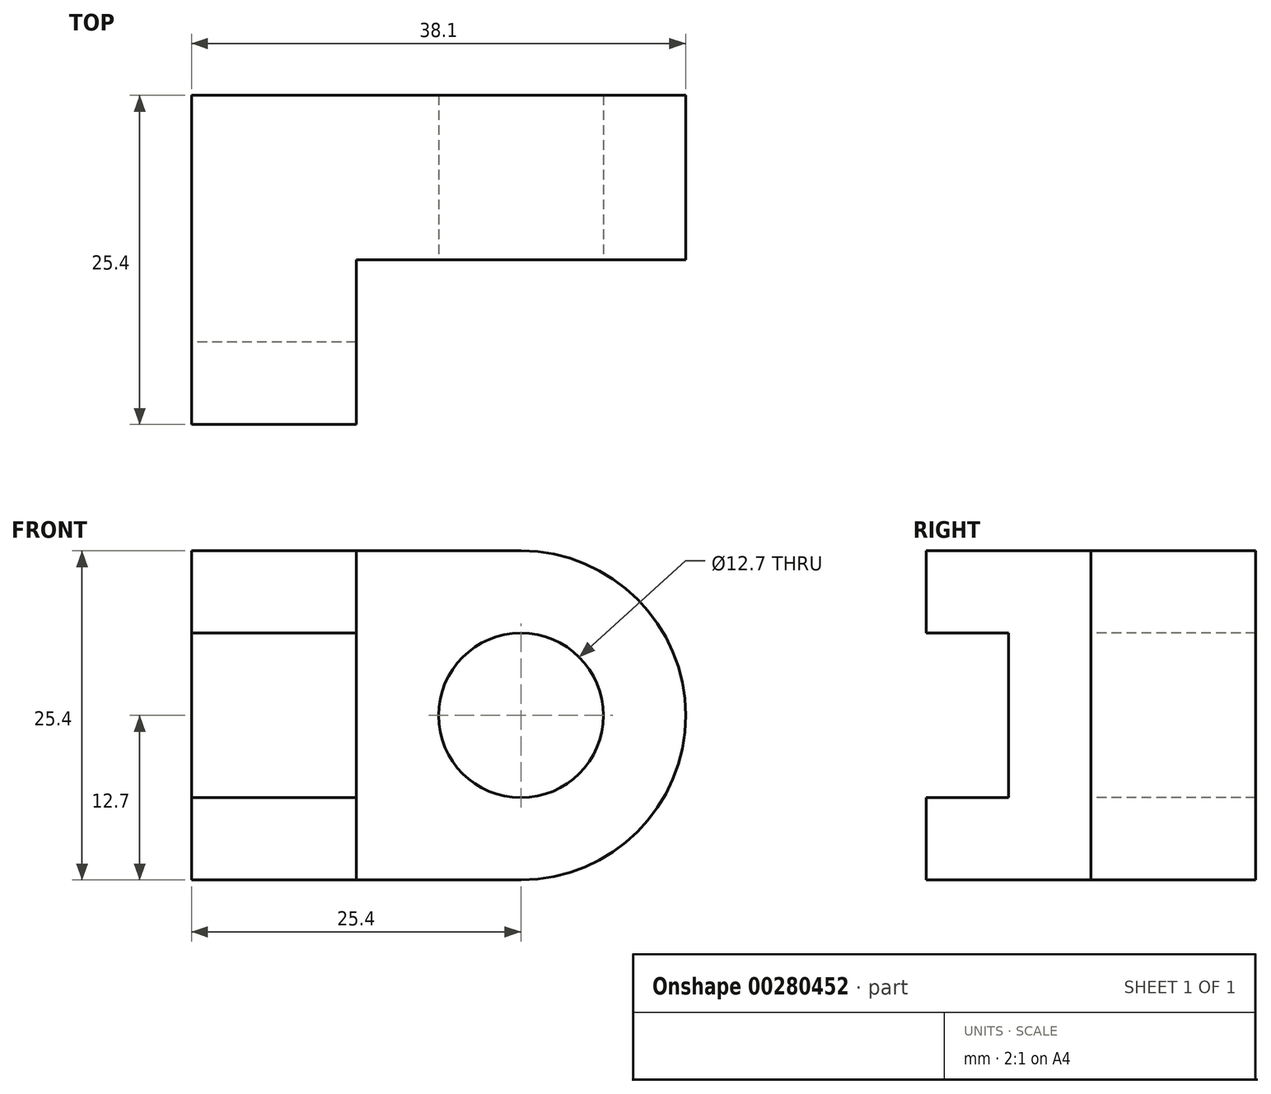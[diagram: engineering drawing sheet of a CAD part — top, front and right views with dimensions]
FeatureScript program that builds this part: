
annotation { "Feature Type Name" : "Feature", "Feature Type Description" : "" }
export const myFeature = defineFeature(function(context is Context, id is Id, definition is map)
    precondition{}
    {
        {
            var Q0;
            Q0=qCreatedBy(makeId("Top.planeOp"),FACE);
            var sketch = newSketch(context, id + "F0", { "sketchPlane" : qUnion([Q0])});
            skLineSegment(sketch, "E0", {"start": v(0, 0) * mm, "end": v(12.7, 0) * mm});
            skLineSegment(sketch, "E1", {"start": v(12.7, 0) * mm, "end": v(12.7, 12.7) * mm});
            skLineSegment(sketch, "E2", {"start": v(12.7, 12.7) * mm, "end": v(38.1, 12.7) * mm});
            skLineSegment(sketch, "E3", {"start": v(38.1, 12.7) * mm, "end": v(38.1, 25.4) * mm});
            skLineSegment(sketch, "E4", {"start": v(38.1, 25.4) * mm, "end": v(0, 25.4) * mm});
            skLineSegment(sketch, "E5", {"start": v(0, 25.4) * mm, "end": v(0, 0) * mm});
            skSolve(sketch);
        }
        {
            var Q0;
            Q0 = qSketchRegion(id + "F0", true);
            extrude(context, id + "F1", {"entities" : qUnion([Q0]), "depth" : 25.4 * mm});
        }
        {
            var Q0;
            Q0=makeQuery(id+"F1.opExtrude","CAP_FACE",FACE,{"disambiguationData":[OSD([sQuery(id+"F0.wireOp",EDGE,"E0"),sQuery(id+"F0.wireOp",EDGE,"E1"),sQuery(id+"F0.wireOp",EDGE,"E2"),sQuery(id+"F0.wireOp",EDGE,"E3"),sQuery(id+"F0.wireOp",EDGE,"E4"),sQuery(id+"F0.wireOp",EDGE,"E5")])],"isStart":false});
            var sketch = newSketch(context, id + "F2", { "sketchPlane" : qUnion([Q0])});
            skLineSegment(sketch, "E6.bottom", {"start": v(12.7, 0) * mm, "end": v(0, 0) * mm});
            skLineSegment(sketch, "E6.top", {"start": v(12.7, 6.35) * mm, "end": v(0, 6.35) * mm});
            skLineSegment(sketch, "E6.left", {"start": v(12.7, 0) * mm, "end": v(12.7, 6.35) * mm});
            skLineSegment(sketch, "E6.right", {"start": v(0, 0) * mm, "end": v(0, 6.35) * mm});
            skSolve(sketch);
        }
        {
            var Q0;
            Q0 = qSketchRegion(id + "F2", true);
            extrude(context, id + "F3", {"entities" : qUnion([Q0]), "operationType" : NewBodyOperationType.REMOVE, "oppositeDirection" : true, "depth" : 19.05 * mm, "hasSecondDirection" : true, "secondDirectionOppositeDirection" : true, "secondDirectionDepth" : 6.35 * mm});
        }
        {
            var Q0;
            Q0=makeQuery(id+"F1.opExtrude","SWEPT_FACE",FACE,{"disambiguationData":[OSD([sQuery(id+"F0.wireOp",EDGE,"E2")])]});
            var sketch = newSketch(context, id + "F4", { "sketchPlane" : qUnion([Q0])});
            skCircle(sketch, "E7", {"center": v(25.4, 12.7) * mm, "radius": 6.35 * mm});
            skLineSegment(sketch, "E8", {"start": v(25.4, 25.4) * mm, "end": v(25.4, 25.4) * mm});
            skLineSegment(sketch, "E9", {"start": v(38.1, 12.7) * mm, "end": v(38.1, 12.7) * mm});
            skLineSegment(sketch, "E10", {"start": v(25.4, 0) * mm, "end": v(25.4, 0) * mm});
            skPoint(sketch, "E11.visualSharp", {"position": v(38.1, 25.4) * mm});
            skArc(sketch, "E11.filletArc", {"start": v(38.1, 12.7) * mm, "mid": v(34.38, 21.68) * mm, "end": v(25.4, 25.4) * mm});
            skPoint(sketch, "E12.visualSharp", {"position": v(38.1, 0) * mm});
            skArc(sketch, "E12.filletArc", {"start": v(25.4, 0) * mm, "mid": v(34.38, 3.72) * mm, "end": v(38.1, 12.7) * mm});
            skLineSegment(sketch, "E13", {"start": v(25.4, 25.4) * mm, "end": v(38.1, 25.4) * mm});
            skLineSegment(sketch, "E14", {"start": v(38.1, 25.4) * mm, "end": v(38.1, 0) * mm});
            skLineSegment(sketch, "E15", {"start": v(38.1, 0) * mm, "end": v(25.4, 0) * mm});
            skSolve(sketch);
        }
        {
            var Q0;
            Q0 = qSketchRegion(id + "F4", true);
            extrude(context, id + "F5", {"entities" : qUnion([Q0]), "operationType" : NewBodyOperationType.REMOVE, "endBound" : BoundingType.THROUGH_ALL, "oppositeDirection" : true, "depth" : 25.4 * mm});
        }
    });
